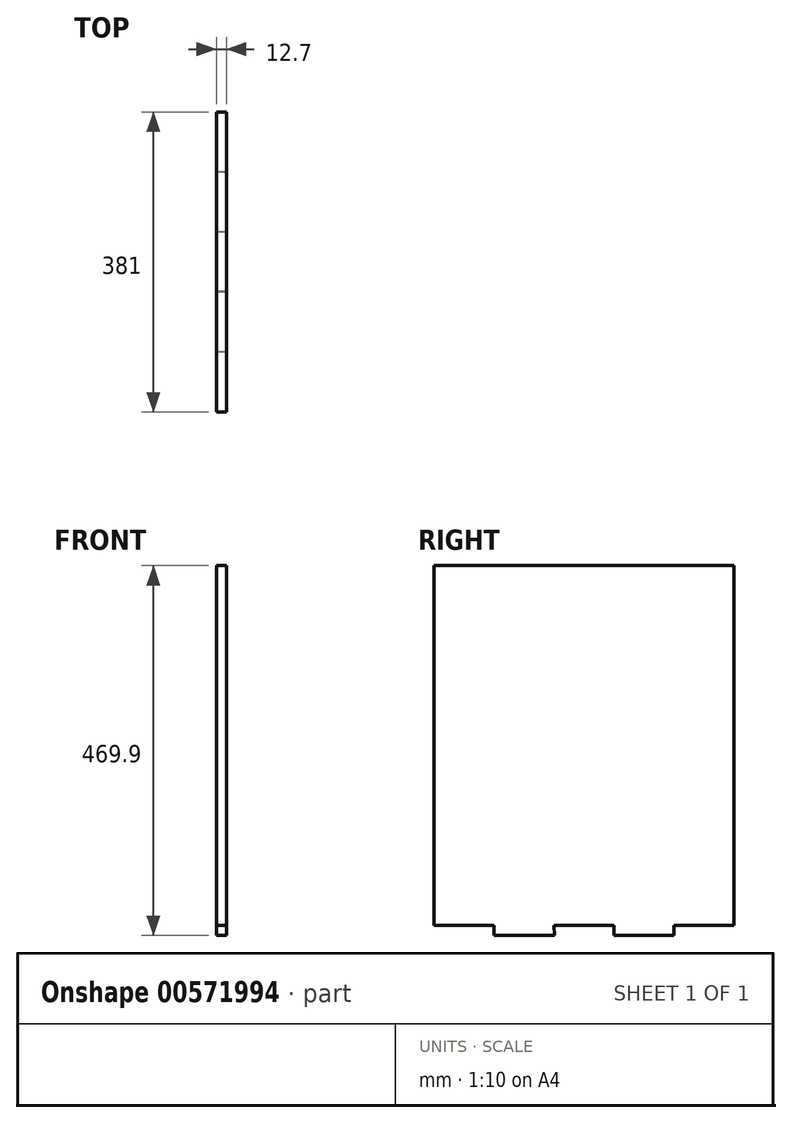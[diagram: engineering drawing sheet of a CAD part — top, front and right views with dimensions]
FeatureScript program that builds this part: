
annotation { "Feature Type Name" : "Feature", "Feature Type Description" : "" }
export const myFeature = defineFeature(function(context is Context, id is Id, definition is map)
    precondition{}
    {
        {
            var Q0;
            Q0=qCreatedBy(makeId("Right.planeOp"),FACE);
            var sketch = newSketch(context, id + "F0", { "sketchPlane" : qUnion([Q0])});
            skLineSegment(sketch, "E0.bottom", {"start": v(-186.87, 161.3) * mm, "end": v(194.13, 161.3) * mm});
            skLineSegment(sketch, "E0.top", {"start": v(-186.87, -295.9) * mm, "end": v(-110.67, -295.9) * mm});
            skLineSegment(sketch, "E0.left", {"start": v(-186.87, 161.3) * mm, "end": v(-186.87, -295.9) * mm});
            skLineSegment(sketch, "E0.right", {"start": v(194.13, 161.3) * mm, "end": v(194.13, -295.9) * mm});
            skLineSegment(sketch, "E1", {"start": v(-110.67, -295.9) * mm, "end": v(-110.67, -308.6) * mm});
            skLineSegment(sketch, "E2", {"start": v(-110.67, -308.6) * mm, "end": v(-33.8, -308.6) * mm});
            skLineSegment(sketch, "E3", {"start": v(-33.8, -308.6) * mm, "end": v(-34.47, -295.9) * mm});
            skLineSegment(sketch, "E4", {"start": v(41.73, -295.9) * mm, "end": v(41.73, -308.6) * mm});
            skLineSegment(sketch, "E5", {"start": v(41.73, -308.6) * mm, "end": v(117.93, -308.6) * mm});
            skLineSegment(sketch, "E6", {"start": v(117.93, -308.6) * mm, "end": v(117.93, -295.9) * mm});
            skLineSegment(sketch, "E7.trimOffspring", {"start": v(-34.47, -295.9) * mm, "end": v(41.73, -295.9) * mm});
            skLineSegment(sketch, "E8.trimOffspring", {"start": v(117.93, -295.9) * mm, "end": v(194.13, -295.9) * mm});
            skSolve(sketch);
        }
        {
            var Q0;
            Q0 = qSketchRegion(id + "F0", true);
            extrude(context, id + "F1", {"entities" : qUnion([Q0]), "depth" : 12.7 * mm, "offsetDistance" : 25.4 * mm});
        }
    });
